# Revit family: Gira_2844600
name_source: partatom
category: Electrical Fixtures
revit_build: Autodesk Revit 2017 (Build: 20160225_1515(x64)
units: mm (PartAtom-declared; Revit-internal decimal feet)

## family parameters
Cut with Voids When Loaded = No
Host = Face
Maintain Annotation Orientation = Yes
Part Type = Normal
Room Calculation Point = No
Round Connector Dimension = Use Diameter
Shared = No

## types (1)
- Rocker btn BS 3-g NO con. System 55 stainl.steel(lac.)
    Assembly arrangement = Basic element with adapter plate
    Available = No
    BIM (1) = https://media.stage.bim.site und Tasten.rfa?public/gira/36a6b08/Sys55_Komplettgerät_Schalten und Tasten.rfa
    Category = Push-switch button
    Colour = Stainless steel
    Data sheet (1) = https://katalog.gira.de
    Default Elevation = 1219 mm
    Description = Rock.btn BS 3g 10A NO con.1-p Sys55 SSTl,British Standard rocker button (BS EN 60669-1), 3-gang 10 A 250 V~ with rockers,System 55, support ring 71 x 71 mm, NO contact 1-pole,stainless steel (lacquered),Features:,- With screw terminals.,,Notes :,- For screw mounting only.
    GTIN = 4010337021957
    HAN = 2844600
    Halogen free = Yes
    HeinzeBIM = https://bimportal.heinze.de
    Imprint = None
    Label space/information surface = No
    Manufacturer = Gira
    Manufacturer URL = https://www.gira.de
    Material = Other
    Material quality = Other
    Method of operation = Rocker
    Model = Group push button
    Mounting method = Flush mounted (plaster)
    Name = Rocker btn BS 3-g NO con. System 55 stainl.steel(lac.)
    Number of rockers = 3
    Suitable for degree of protection (IP) = IP20
    Surface protection = Other
    Transparent = No
    Type of fastening = Mounting with claw and screw
    URL = http://katalog.gira.de
    With lighting = No

## geometry (parser evidence)
native form markers: Sweep x11
no freeform markers — native parametric forms only
